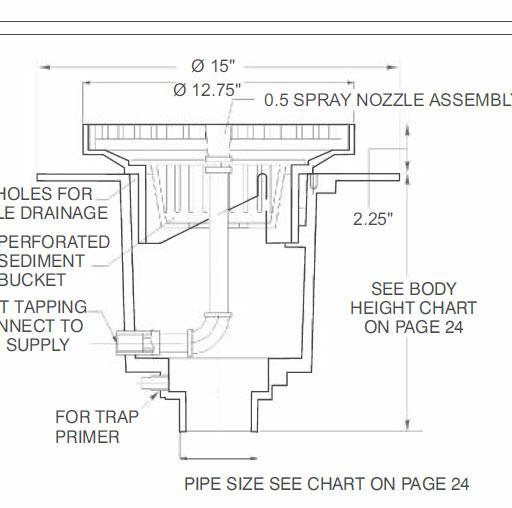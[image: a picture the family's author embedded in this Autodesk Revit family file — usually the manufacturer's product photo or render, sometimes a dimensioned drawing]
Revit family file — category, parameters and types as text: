
# Revit family: F1350-Y-36
name_source: partatom
category: Plumbing Fixtures
revit_build: Autodesk Revit 2018 (Build: 20170223_1515(x64)
units: mm (PartAtom-declared; Revit-internal decimal feet)

## family parameters
Cut with Voids When Loaded = No
Host = Face
Part Type = Normal
Room Calculation Point = No
Round Connector Dimension = Use Radius
Shared = No

## types (5) — shared parameters
Default Elevation = 0' - 0"
Description = GARBAGE CAN WASH DRAIN WITH 12" ROUND HEAVY DUTY TRACTOR GRATE & EXTRA DEEP SUMP
Floor Drain Material = Paint - Sherwin Williams Paint - #952C2A - Bellwood Red
Manufacturer = MIFAB
Model = F1350-Y-36
URL = WWW.MIFAB.COM
zero-valued in all types: CWFU, WFU

## per-type parameters (varying)
| type | Body Height | Pipe Diameter | Pipe Radius |
| 4" Drain Pipe Size | 1' - 0 1/2" | 0' - 4" | 0' - 2" |
| 2" Drain Pipe Size | 1' - 0 1/4" | 0' - 2" | 0' - 1" |
| 3" Drain Pipe Size | 1' - 0 1/4" | 0' - 3" | 0' - 1 1/2" |
| 5" Drain Pipe Size | 1' - 0 1/2" | 0' - 5" | 0' - 2 1/2" |
| 6" Drain Pipe Size | 1' - 0 3/4" | 0' - 6" | 0' - 3" |

## geometry (parser evidence)
native form markers: Blend x2, Sweep x9
no freeform markers — native parametric forms only
